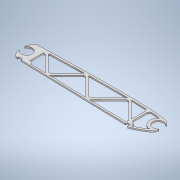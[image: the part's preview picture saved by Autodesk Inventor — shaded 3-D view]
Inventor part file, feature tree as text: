
AUTODESK INVENTOR PART (.ipt)
format: ipt  version: 2022 (Build 260153000, 153)  size: 382,464 bytes
history: native  units: mm
features: extrude x1, sketch x1
ambient origin geometry x8: Origin, YZ Plane, XZ Plane, XY Plane, X Axis, Y Axis, Z Axis, Center Point
bodies: Body1 (feature_tree)
feature tree (2):
  extrude  "Extrusion5"  Depth=368.759386mm
  sketch  "Sketch1"  dims[d31=34.456mm d50=368.759386mm d57=16.0mm d69=8.0mm d70=23.0mm d71=8.0mm d73=16.0mm d80=19.0mm d81=16.0mm d82=1.0mm d83=1.0mm d84=1.0mm d85=1.0mm d86=1.0mm d87=0.8mm d88=1.0mm d90=19.0mm d94=5.0mm d95=5.0mm d105=5.0mm d106=5.0mm d108=2.0mm d109=19.0mm d114=5.0mm d115=5.0mm d116=24.0mm d117=2.5mm d118=2.5mm d123=2.5mm d124=2.5mm d125=10.0mm d126=24.0mm d127=24.0mm d128=27.0mm d135=0.5mm d136=45.0deg d139=7.0mm d165=45.0deg d169=27.0mm d175=90.0deg d181=45.0deg d185=7.0mm d186=45.0deg d190=7.0mm d191=45.0deg d197=90.0deg d203=90.0deg d206=7.0mm d207=2.0mm d208=0.0mm]
